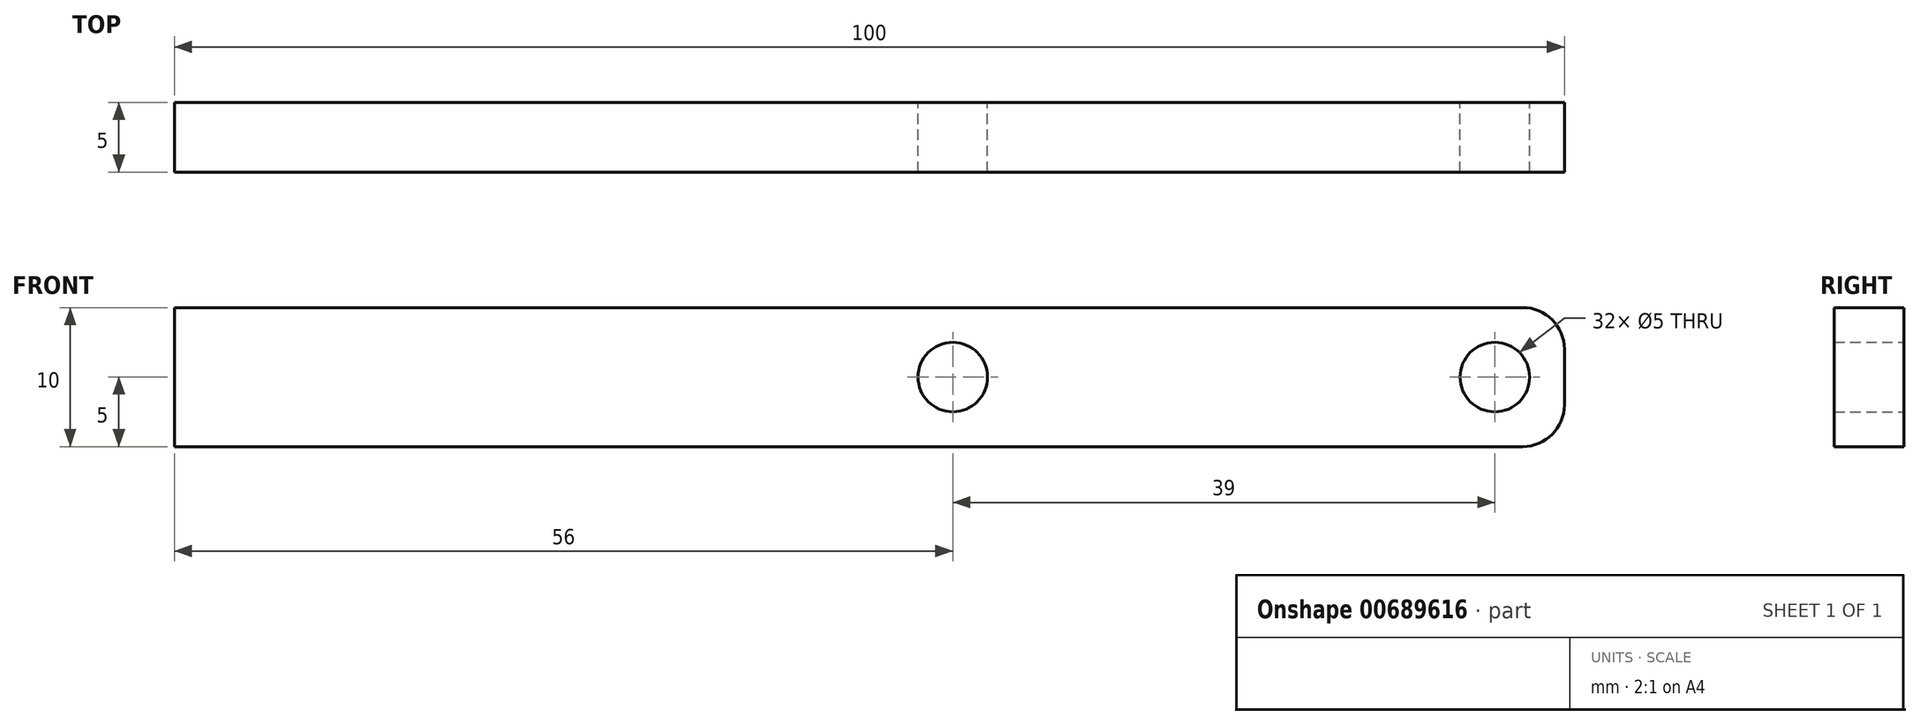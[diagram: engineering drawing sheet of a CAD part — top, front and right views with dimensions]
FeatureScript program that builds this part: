
annotation { "Feature Type Name" : "Feature", "Feature Type Description" : "" }
export const myFeature = defineFeature(function(context is Context, id is Id, definition is map)
    precondition{}
    {
        {
            var Q0;
            Q0=qCreatedBy(makeId("Front.planeOp"),FACE);
            var sketch = newSketch(context, id + "F0", { "sketchPlane" : qUnion([Q0])});
            skLineSegment(sketch, "E0", {"start": v(0, 0) * mm, "end": v(97, 0) * mm});
            skLineSegment(sketch, "E1", {"start": v(100, 3) * mm, "end": v(100, 7) * mm});
            skLineSegment(sketch, "E2", {"start": v(97, 10) * mm, "end": v(0, 10) * mm});
            skLineSegment(sketch, "E3", {"start": v(0, 10) * mm, "end": v(0, 0) * mm});
            skCircle(sketch, "E4", {"center": v(95, 5) * mm, "radius": 2.5 * mm});
            skCircle(sketch, "E5", {"center": v(56, 5) * mm, "radius": 2.5 * mm});
            skArc(sketch, "E6.filletArc", {"start": v(100, 7) * mm, "mid": v(99.12, 9.12) * mm, "end": v(97, 10) * mm});
            skArc(sketch, "E7.filletArc", {"start": v(97, 0) * mm, "mid": v(99.12, 0.88) * mm, "end": v(100, 3) * mm});
            skSolve(sketch);
        }
        {
            var Q0;
            Q0=makeQuery(id+"F0.imprint","IMPRINT",FACE,{"disambiguationData":[TD([[makeQuery(id+"F0.imprint","IMPRINT",EDGE,{"derivedFrom":sQuery(id+"F0.wireOp",EDGE,"E0")}),1.0]])]});
            extrude(context, id + "F1", {"entities" : qUnion([Q0]), "depth" : 5 * mm, "offsetDistance" : 25 * mm});
        }
    });
